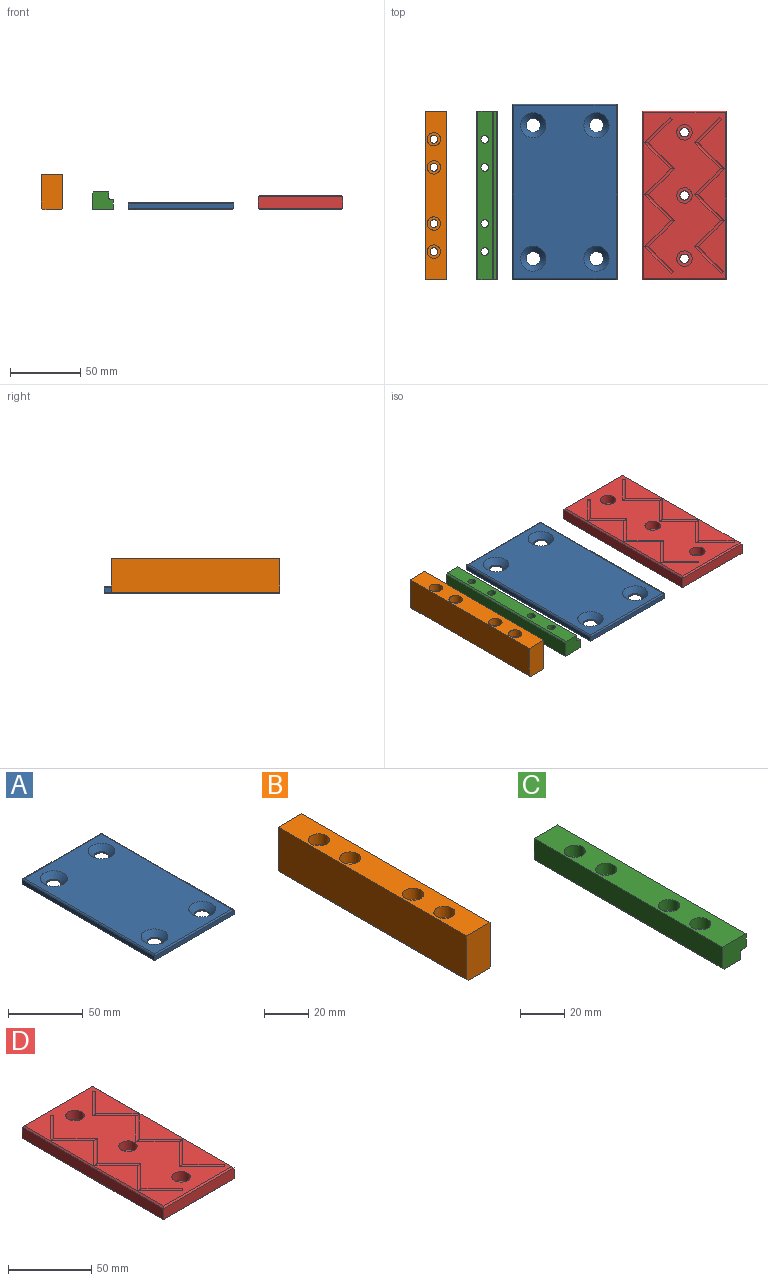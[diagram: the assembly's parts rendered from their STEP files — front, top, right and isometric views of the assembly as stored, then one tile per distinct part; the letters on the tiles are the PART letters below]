
ASSEMBLY  parts=4 mates=6
PART A: 22 faces, bbox 75x125x5 mm
  f0: cylinder r=1mm len=75mm, axis (-1,0,0), area 116.7mm2, adj f1,f2,f5,f20
  f1: cylinder r=1mm len=125mm, axis (0,1,0), area 195.2mm2, adj f0,f2,f3,f21
  f2: plane 123x73mm, normal (0,0,1), area 7961.1mm2, adj f0,f1,f3,f5,f12,f14,f16,f18
  f3: cylinder r=1mm len=75mm, axis (1,0,0), area 116.7mm2, adj f1,f2,f4,f5
  f4: plane 75x3.5mm, normal (0,-1,0), area 262.5mm2, adj f3,f9,f19,f21
  f5: cylinder r=1mm len=125mm, axis (0,-1,0), area 195.2mm2, adj f0,f2,f3,f19
  f6: plane 75x0.5mm, normal (0,0.71,-0.71), area 52.7mm2, adj f7,f8,f10,f20
  f7: plane 124x74mm, normal (0,0,-1), area 8861.8mm2, adj f6,f8,f9,f10,f11,f13,f15,f17
  f8: plane 125x0.5mm, normal (0.71,0,-0.71), area 88mm2, adj f6,f7,f9,f21
  f9: plane 75x0.5mm, normal (0,-0.71,-0.71), area 52.7mm2, adj f4,f7,f8,f10
  f10: plane 125x0.5mm, normal (-0.71,0,-0.71), area 88mm2, adj f6,f7,f9,f19
  f11: cylinder r=5mm len=10mm, axis (0,0,1), area 31.4mm2, adj f7,f12
  f12: cone r=7mm half-angle=45deg, axis (0,0,1), area 248.8mm2, adj f2,f11
  f13: cylinder r=5mm len=10mm, axis (0,0,1), area 31.4mm2, adj f7,f14
  f14: cone r=7mm half-angle=45deg, axis (0,0,1), area 248.8mm2, adj f2,f13
  f15: cylinder r=5mm len=10mm, axis (0,0,1), area 31.4mm2, adj f7,f16
  f16: cone r=7mm half-angle=45deg, axis (0,0,1), area 248.8mm2, adj f2,f15
  f17: cylinder r=5mm len=10mm, axis (0,0,1), area 31.4mm2, adj f7,f18
  f18: cone r=7mm half-angle=45deg, axis (0,0,1), area 248.8mm2, adj f2,f17
  f19: plane 125x3.5mm, normal (-1,0,0), area 437.5mm2, adj f4,f5,f10,f20
  f20: plane 75x3.5mm, normal (0,1,0), area 262.5mm2, adj f0,f6,f19,f21
  f21: plane 125x3.5mm, normal (1,0,0), area 437.5mm2, adj f1,f4,f8,f20
PART B: 28 faces, bbox 15x120x25 mm
  f0: plane 120x0.5mm, normal (0.71,0,-0.71), area 84.9mm2, adj f1,f2,f26,f27
  f1: plane 120x13.5mm, normal (0,0,-1), area 1525mm2, adj f0,f2,f3,f12,f15,f18,f21,f26
  f2: plane 25x15mm, normal (0,-1,0), area 374.4mm2, adj f0,f1,f3,f24,f25,f27
  f3: plane 120x1mm, normal (-0.71,0,-0.71), area 169.7mm2, adj f1,f2,f25,f26
  f4: cylinder r=1.25mm len=21.12mm, axis (0,0.71,0.71), area 62.3mm2, adj f5,f11,f27
  f5: cylinder r=1.25mm len=21.83mm, axis (0,0.71,-0.71), area 62.3mm2, adj f4,f6,f27
  f6: cylinder r=1.25mm len=21.83mm, axis (0,0.71,0.71), area 62.3mm2, adj f5,f7,f27
  f7: cylinder r=1.25mm len=21.83mm, axis (0,0.71,-0.71), area 62.3mm2, adj f6,f8,f27
  f8: cylinder r=1.25mm len=21.83mm, axis (0,0.71,0.71), area 62.3mm2, adj f7,f10,f27
  f9: plane 1.41x1.41mm, normal (0,-0.71,0.71), area 0.7mm2, adj f10,f27
  f10: cylinder r=1.25mm len=17.12mm, axis (0,0.71,-0.71), area 49.2mm2, adj f8,f9,f27
  f11: plane 1.41x1.41mm, normal (0,0.71,0.71), area 0.7mm2, adj f4,f27
  f12: cylinder r=2.75mm len=19mm, axis (0,0,1), area 328.3mm2, adj f1,f14
  f13: cylinder r=4.75mm len=9.5mm, axis (0,0,1), area 179.1mm2, adj f14,f24
  f14: plane 9.5x9.5mm, normal (0,0,1), area 47.1mm2, adj f12,f13
  f15: cylinder r=2.75mm len=19mm, axis (0,0,1), area 328.3mm2, adj f1,f17
  f16: cylinder r=4.75mm len=9.5mm, axis (0,0,1), area 179.1mm2, adj f17,f24
  f17: plane 9.5x9.5mm, normal (0,0,1), area 47.1mm2, adj f15,f16
  f18: cylinder r=2.75mm len=19mm, axis (0,0,1), area 328.3mm2, adj f1,f20
  f19: cylinder r=4.75mm len=9.5mm, axis (0,0,1), area 179.1mm2, adj f20,f24
  f20: plane 9.5x9.5mm, normal (0,0,1), area 47.1mm2, adj f18,f19
  f21: cylinder r=2.75mm len=19mm, axis (0,0,1), area 328.3mm2, adj f1,f23
  f22: cylinder r=4.75mm len=9.5mm, axis (0,0,1), area 179.1mm2, adj f23,f24
  f23: plane 9.5x9.5mm, normal (0,0,1), area 47.1mm2, adj f21,f22
  f24: plane 120x15mm, normal (0,0,1), area 1516.5mm2, adj f2,f13,f16,f19,f22,f25,f26,f27
  f25: plane 120x24mm, normal (-1,0,0), area 2880mm2, adj f2,f3,f24,f26
  f26: plane 25x15mm, normal (0,1,0), area 374.4mm2, adj f0,f1,f3,f24,f25,f27
  f27: plane 120x24.5mm, normal (1,0,0), area 2628.9mm2, adj f0,f2,f4,f5,f6,f7,f8,f9
PART C: 23 faces, bbox 15x120x12.5 mm
  f0: cylinder r=0.8mm len=120mm, axis (0,-1,0), area 150.8mm2, adj f1,f4,f7,f21
  f1: plane 120x2.2mm, normal (0,0,-1), area 264mm2, adj f0,f2,f4,f21
  f2: plane 120x0.5mm, normal (0.71,0,-0.71), area 84.9mm2, adj f1,f3,f4,f21
  f3: plane 120x7mm, normal (1,0,0), area 840mm2, adj f2,f4,f20,f21
  f4: plane 15x12.5mm, normal (0,1,0), area 169.5mm2, adj f0,f1,f2,f3,f5,f6,f7,f20
  f5: plane 120x1mm, normal (-0.71,0,-0.71), area 169.7mm2, adj f4,f6,f21,f22
  f6: plane 120x10.5mm, normal (0,0,-1), area 1165mm2, adj f4,f5,f7,f8,f11,f14,f17,f21
  f7: plane 120x4.2mm, normal (1,0,0), area 504mm2, adj f0,f4,f6,f21
  f8: cylinder r=2.75mm len=6.5mm, axis (0,0,1), area 112.3mm2, adj f6,f10
  f9: cylinder r=4.75mm len=9.5mm, axis (0,0,1), area 179.1mm2, adj f10,f20
  f10: plane 9.5x9.5mm, normal (0,0,1), area 47.1mm2, adj f8,f9
  f11: cylinder r=2.75mm len=6.5mm, axis (0,0,1), area 112.3mm2, adj f6,f13
  f12: cylinder r=4.75mm len=9.5mm, axis (0,0,1), area 179.1mm2, adj f13,f20
  f13: plane 9.5x9.5mm, normal (0,0,1), area 47.1mm2, adj f11,f12
  f14: cylinder r=2.75mm len=6.5mm, axis (0,0,1), area 112.3mm2, adj f6,f16
  f15: cylinder r=4.75mm len=9.5mm, axis (0,0,1), area 179.1mm2, adj f16,f20
  f16: plane 9.5x9.5mm, normal (0,0,1), area 47.1mm2, adj f14,f15
  f17: cylinder r=2.75mm len=6.5mm, axis (0,0,1), area 112.3mm2, adj f6,f19
  f18: cylinder r=4.75mm len=9.5mm, axis (0,0,1), area 179.1mm2, adj f19,f20
  f19: plane 9.5x9.5mm, normal (0,0,1), area 47.1mm2, adj f17,f18
  f20: plane 120x15mm, normal (0,0,1), area 1516.5mm2, adj f3,f4,f9,f12,f15,f18,f21,f22
  f21: plane 15x12.5mm, normal (0,-1,0), area 169.5mm2, adj f0,f1,f2,f3,f5,f6,f7,f20
  f22: plane 120x11.5mm, normal (-1,0,0), area 1380mm2, adj f4,f5,f20,f21
PART D: 39 faces, bbox 60x120x10 mm
  f0: cylinder r=1.25mm len=20.62mm, axis (-0.71,0.71,0), area 60.7mm2, adj f1,f7,f18
  f1: cylinder r=1.25mm len=21.33mm, axis (0.71,0.71,0), area 60.7mm2, adj f0,f2,f18
  f2: cylinder r=1.25mm len=21.33mm, axis (-0.71,0.71,0), area 60.7mm2, adj f1,f3,f18
  f3: cylinder r=1.25mm len=21.33mm, axis (0.71,0.71,0), area 60.7mm2, adj f2,f4,f18
  f4: cylinder r=1.25mm len=21.33mm, axis (-0.71,0.71,0), area 60.7mm2, adj f3,f6,f18
  f5: plane 1.41x1.41mm, normal (-0.71,-0.71,0), area 0.7mm2, adj f6,f18
  f6: cylinder r=1.25mm len=19.62mm, axis (0.71,0.71,0), area 57.4mm2, adj f4,f5,f18
  f7: plane 1.41x1.41mm, normal (-0.71,0.71,0), area 0.7mm2, adj f0,f18
  f8: cylinder r=1.25mm len=20.62mm, axis (-0.71,0.71,0), area 60.7mm2, adj f9,f15,f18
  f9: cylinder r=1.25mm len=21.33mm, axis (0.71,0.71,0), area 60.7mm2, adj f8,f10,f18
  f10: cylinder r=1.25mm len=21.33mm, axis (-0.71,0.71,0), area 60.7mm2, adj f9,f11,f18
  f11: cylinder r=1.25mm len=21.33mm, axis (0.71,0.71,0), area 60.7mm2, adj f10,f12,f18
  f12: cylinder r=1.25mm len=21.33mm, axis (-0.71,0.71,0), area 60.7mm2, adj f11,f14,f18
  f13: plane 1.41x1.41mm, normal (-0.71,-0.71,0), area 0.7mm2, adj f14,f18
  f14: cylinder r=1.25mm len=19.62mm, axis (0.71,0.71,0), area 57.4mm2, adj f12,f13,f18
  f15: plane 1.41x1.41mm, normal (-0.71,0.71,0), area 0.7mm2, adj f8,f18
  f16: plane 60x1mm, normal (0,0.71,0.71), area 83.4mm2, adj f17,f18,f21,f37
  f17: plane 120x1mm, normal (0.71,0,0.71), area 168.3mm2, adj f16,f18,f19,f38
  f18: plane 118x58mm, normal (0,0,1), area 5936.6mm2, adj f0,f1,f2,f3,f4,f5,f6,f7
  f19: plane 60x1mm, normal (0,-0.71,0.71), area 83.4mm2, adj f17,f18,f20,f21
  f20: plane 60x8mm, normal (0,-1,0), area 480mm2, adj f19,f25,f36,f38
  f21: plane 120x1mm, normal (-0.71,0,0.71), area 168.3mm2, adj f16,f18,f19,f36
  f22: plane 60x1mm, normal (0,0.71,-0.71), area 83.4mm2, adj f23,f24,f26,f37
  f23: plane 118x58mm, normal (0,0,-1), area 6741.4mm2, adj f22,f24,f25,f26,f27,f30,f33
  f24: plane 120x1mm, normal (0.71,0,-0.71), area 168.3mm2, adj f22,f23,f25,f38
  f25: plane 60x1mm, normal (0,-0.71,-0.71), area 83.4mm2, adj f20,f23,f24,f26
  f26: plane 120x1mm, normal (-0.71,0,-0.71), area 168.3mm2, adj f22,f23,f25,f36
  f27: cylinder r=3.3mm len=6.6mm, axis (0,0,1), area 72.6mm2, adj f23,f29
  f28: cylinder r=5.5mm len=11mm, axis (0,0,1), area 224.6mm2, adj f18,f29
  f29: plane 11x11mm, normal (0,0,1), area 60.8mm2, adj f27,f28
  f30: cylinder r=3.3mm len=6.6mm, axis (0,0,1), area 72.6mm2, adj f23,f32
  f31: cylinder r=5.5mm len=11mm, axis (0,0,1), area 224.6mm2, adj f18,f32
  f32: plane 11x11mm, normal (0,0,1), area 60.8mm2, adj f30,f31
  f33: cylinder r=3.3mm len=6.6mm, axis (0,0,1), area 72.6mm2, adj f23,f35
  f34: cylinder r=5.5mm len=11mm, axis (0,0,1), area 224.6mm2, adj f18,f35
  f35: plane 11x11mm, normal (0,0,1), area 60.8mm2, adj f33,f34
  f36: plane 120x8mm, normal (-1,0,0), area 960mm2, adj f20,f21,f26,f37
  f37: plane 60x8mm, normal (0,1,0), area 480mm2, adj f16,f22,f36,f38
  f38: plane 120x8mm, normal (1,0,0), area 960mm2, adj f17,f20,f24,f37
PLACE A t=(31.5,73.75,-15.87)mm
PLACE B t=(-30.34,71.25,-15.87)mm
PLACE C rot(axis=(1,0,0),180deg) t=(5.97,71.25,-3.37)mm
PLACE D t=(124.2,71.25,-15.87)mm
MATE planar A.f7 <-> D.f27  axis (0,0,-1) through (69,73.75,-15.87)mm
MATE planar C.f20 <-> A.f7  axis (0,0,-1) through (13.75,71.25,-15.87)mm
MATE planar A.f4 <-> D.f20  axis (0,-1,0) through (69,11.25,-13.62)mm
MATE planar B.f2 <-> C.f4  axis (0,-1,0) through (-22.84,11.25,-3.35)mm
MATE planar C.f4 <-> A.f4  axis (0,-1,0) through (12.9,11.25,-10.02)mm
MATE planar B.f18 <-> C.f11  axis (0,0,-1) through (-24.34,51.25,-15.87)mm
